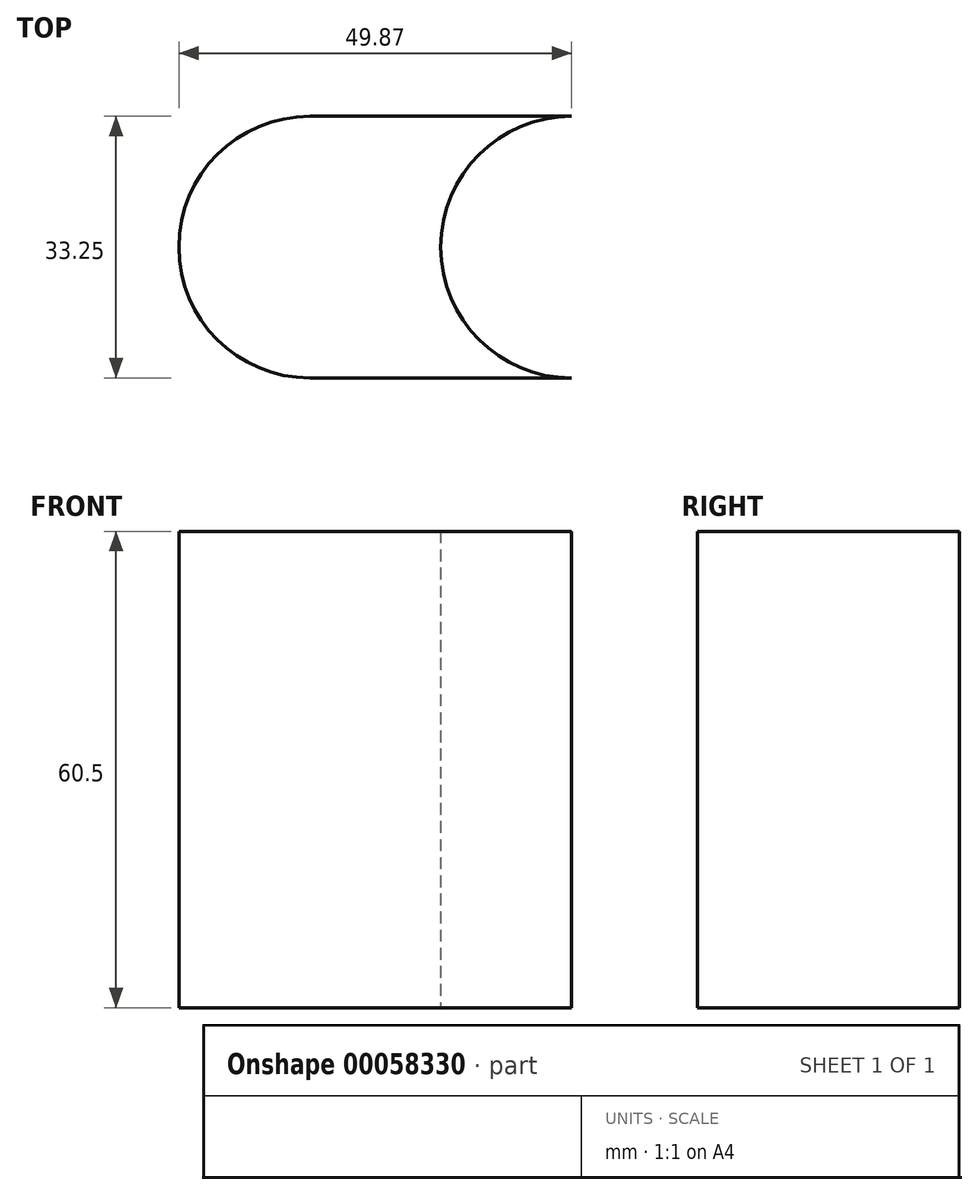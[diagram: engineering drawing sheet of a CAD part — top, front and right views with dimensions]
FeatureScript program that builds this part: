
annotation { "Feature Type Name" : "Feature", "Feature Type Description" : "" }
export const myFeature = defineFeature(function(context is Context, id is Id, definition is map)
    precondition{}
    {
        {
            var Q0;
            Q0=qCreatedBy(makeId("Top.planeOp"),FACE);
            var sketch = newSketch(context, id + "F0", { "sketchPlane" : qUnion([Q0])});
            skCircle(sketch, "E0", {"center": v(0, 0) * mm, "radius": 16.62 * mm});
            skCircle(sketch, "E1.MirrorC", {"center": v(33.25, 0) * mm, "radius": 16.62 * mm});
            skLineSegment(sketch, "E2", {"start": v(0, 16.62) * mm, "end": v(33.25, 16.62) * mm});
            skLineSegment(sketch, "E3", {"start": v(0, -16.62) * mm, "end": v(33.25, -16.62) * mm});
            skSolve(sketch);
        }
        {
            var Q0;
            {var subQ0=sQuery(id+"F0.wireOp",EDGE,"E0");var subQ1=makeQuery(id+"F0.imprint","INTERSECT",VERTEX,{"derivedFrom":[subQ0,sQuery(id+"F0.wireOp",EDGE,"E2")]});Q0=makeQuery(id+"F0.imprint","IMPRINT",FACE,{"disambiguationData":[TD([[makeQuery(id+"F0.imprint","IMPRINT",EDGE,{"disambiguationData":[TD([[subQ1,1.0]])],"derivedFrom":subQ0}),1.0]])]});}
            var Q1;
            {var subQ0=sQuery(id+"F0.wireOp",EDGE,"E2");Q1=makeQuery(id+"F0.imprint","IMPRINT",FACE,{"disambiguationData":[TD([[makeQuery(id+"F0.imprint","IMPRINT",EDGE,{"derivedFrom":subQ0}),-1.0]])]});}
            var Q2;
            {var subQ0=sQuery(id+"F0.wireOp",EDGE,"E1.MirrorC");var subQ1=makeQuery(id+"F0.imprint","INTERSECT",VERTEX,{"derivedFrom":[subQ0,sQuery(id+"F0.wireOp",EDGE,"E2")]});Q2=makeQuery(id+"F0.imprint","IMPRINT",FACE,{"disambiguationData":[TD([[makeQuery(id+"F0.imprint","IMPRINT",EDGE,{"disambiguationData":[TD([[subQ1,1.0]])],"derivedFrom":subQ0}),-1.0]])]});}
            var Q3;
            {var subQ0=sQuery(id+"F0.wireOp",EDGE,"E3");Q3=makeQuery(id+"F0.imprint","IMPRINT",FACE,{"disambiguationData":[TD([[makeQuery(id+"F0.imprint","IMPRINT",EDGE,{"derivedFrom":subQ0}),1.0]])]});}
            extrude(context, id + "F1", {"entities" : qUnion([Q0, Q1, Q2, Q3]), "depth" : 60.5 * mm});
        }
    });
